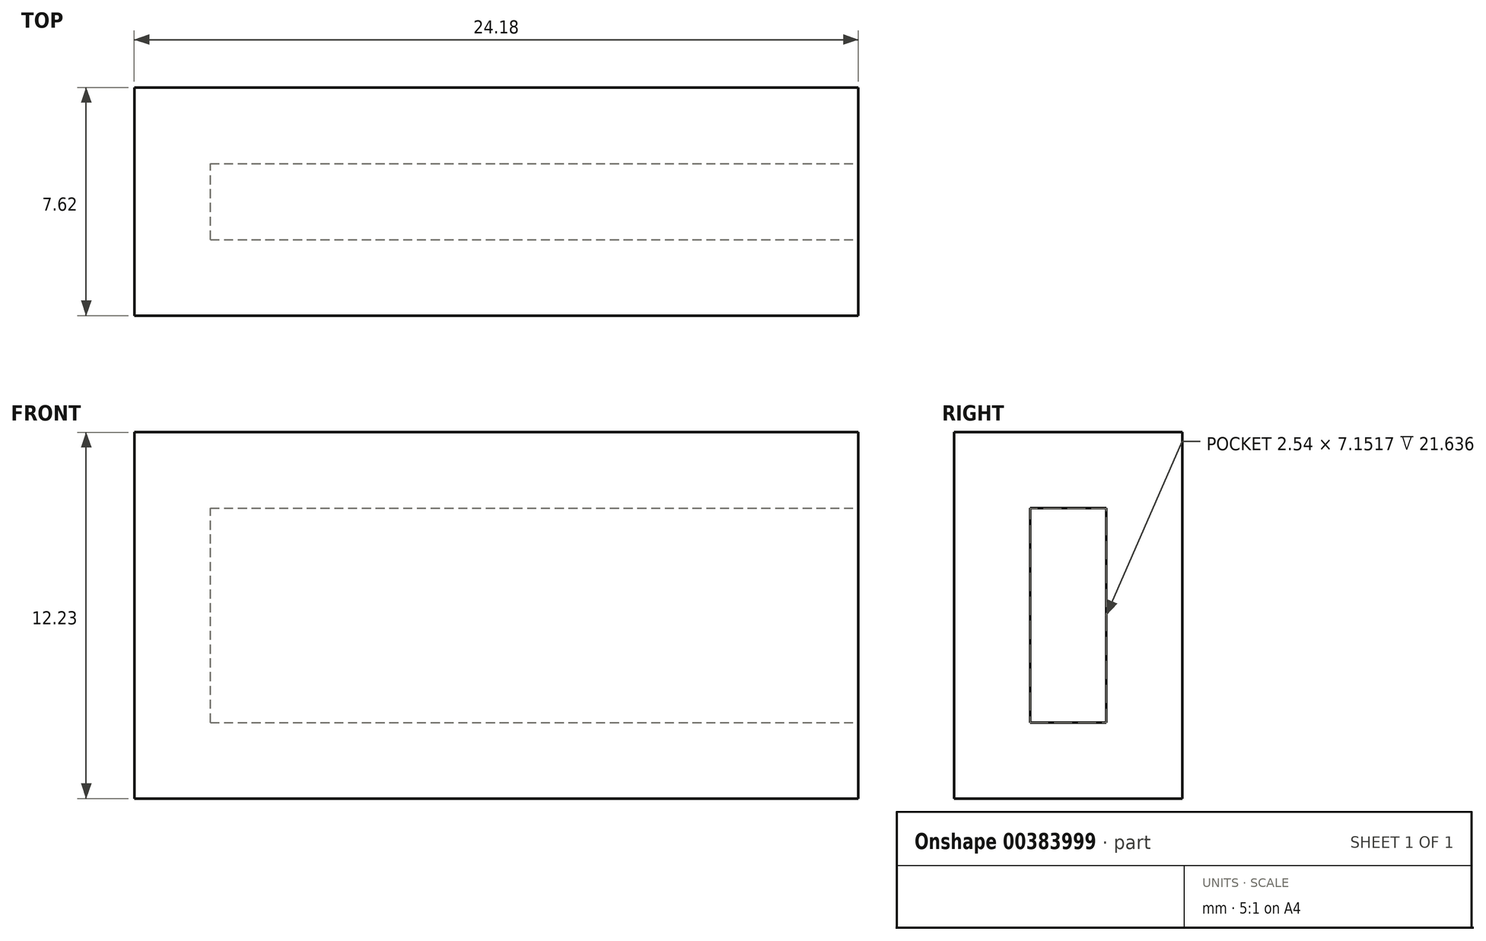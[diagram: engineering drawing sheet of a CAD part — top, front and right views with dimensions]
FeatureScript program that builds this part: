
annotation { "Feature Type Name" : "Feature", "Feature Type Description" : "" }
export const myFeature = defineFeature(function(context is Context, id is Id, definition is map)
    precondition{}
    {
        {
            var Q0;
            Q0=qCreatedBy(makeId("Front.planeOp"),FACE);
            var sketch = newSketch(context, id + "F0", { "sketchPlane" : qUnion([Q0])});
            skLineSegment(sketch, "E0.bottom", {"start": v(-10.22, 0) * mm, "end": v(13.96, 0) * mm});
            skLineSegment(sketch, "E0.top", {"start": v(-10.22, 12.23) * mm, "end": v(13.96, 12.23) * mm});
            skLineSegment(sketch, "E0.left", {"start": v(-10.22, 0) * mm, "end": v(-10.22, 12.23) * mm});
            skLineSegment(sketch, "E0.right", {"start": v(13.96, 0) * mm, "end": v(13.96, 12.23) * mm});
            skSolve(sketch);
        }
        {
            var Q0;
            Q0=makeQuery(id+"F0.imprint","IMPRINT",FACE,{"disambiguationData":[TD([[makeQuery(id+"F0.imprint","IMPRINT",EDGE,{"derivedFrom":sQuery(id+"F0.wireOp",EDGE,"E0.bottom")}),1.0]])]});
            extrude(context, id + "F1", {"entities" : qUnion([Q0]), "depth" : 7.62 * mm, "offsetDistance" : 25.4 * mm});
        }
        {
            var Q0;
            Q0=makeQuery(id+"F1.opExtrude","SWEPT_FACE",FACE,{"disambiguationData":[OSD([sQuery(id+"F0.wireOp",EDGE,"E0.right")])]});
            shell(context, id + "F2", {"entities" : qUnion([Q0]), "thickness" : 2.54 * mm});
        }
    });
